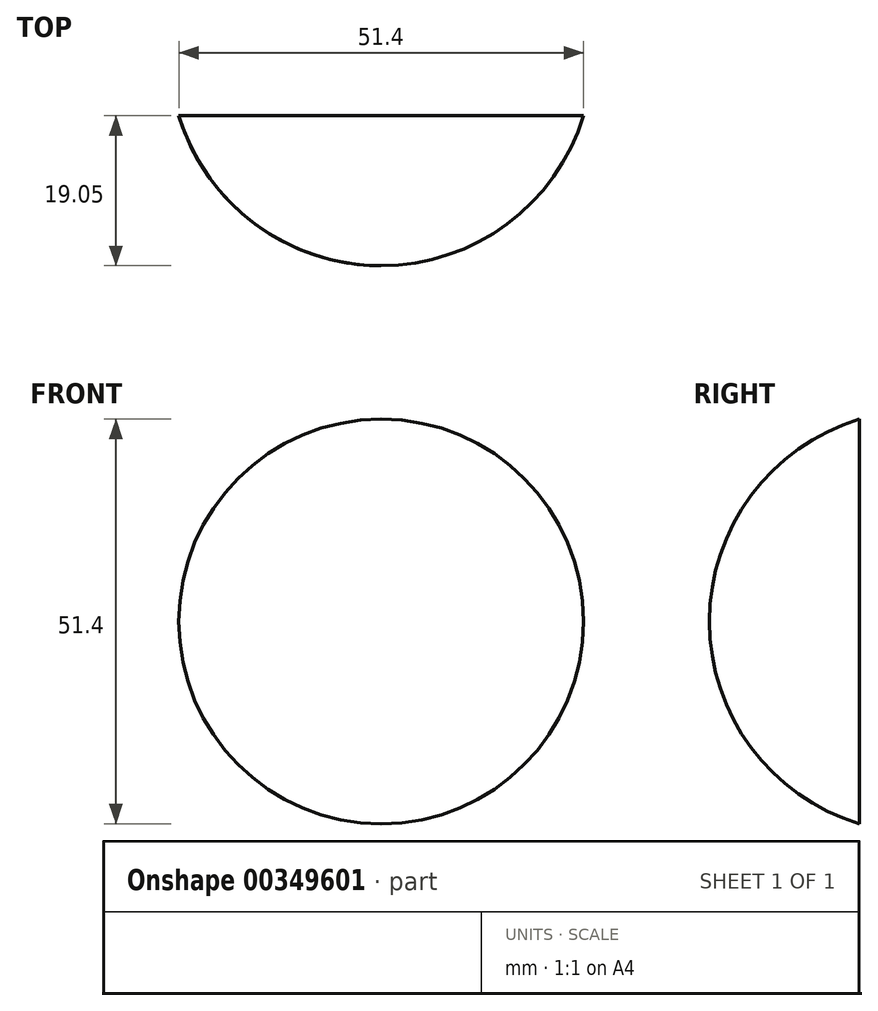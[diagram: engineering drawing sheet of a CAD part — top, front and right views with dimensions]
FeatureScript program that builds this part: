
annotation { "Feature Type Name" : "Feature", "Feature Type Description" : "" }
export const myFeature = defineFeature(function(context is Context, id is Id, definition is map)
    precondition{}
    {
        {
            var Q0;
            Q0=qCreatedBy(makeId("Front.planeOp"),FACE);
            var sketch = newSketch(context, id + "F0", { "sketchPlane" : qUnion([Q0])});
            skCircle(sketch, "E0", {"center": v(0, 0) * mm, "radius": 25.7 * mm});
            skLineSegment(sketch, "E1", {"start": v(-25.7, 0) * mm, "end": v(25.7, 0) * mm});
            skLineSegment(sketch, "E2", {"start": v(0, -25.7) * mm, "end": v(0, 25.7) * mm});
            skSolve(sketch);
        }
        {
            var Q0;
            Q0=qCreatedBy(makeId("Top.planeOp"),FACE);
            var sketch = newSketch(context, id + "F1", { "sketchPlane" : qUnion([Q0])});
            skLineSegment(sketch, "E3", {"start": v(0, 0) * mm, "end": v(0, -19.05) * mm});
            skPoint(sketch, "E4", {"position": v(-25.7, 0) * mm});
            skPoint(sketch, "E5", {"position": v(0, -19.05) * mm});
            skPoint(sketch, "E6", {"position": v(25.7, 0) * mm});
            skArc(sketch, "E7", {"start": v(-25.7, 0) * mm, "mid": v(-16, -13.77) * mm, "end": v(0, -19.05) * mm});
            skLineSegment(sketch, "E8", {"start": v(0, -19.05) * mm, "end": v(0, -44.45) * mm});
            skLineSegment(sketch, "E9", {"start": v(0, -19.05) * mm, "end": v(0, -19.05) * mm});
            skArc(sketch, "E10", {"start": v(0, -19.05) * mm, "mid": v(16, -13.77) * mm, "end": v(25.7, 0) * mm});
            skLineSegment(sketch, "E11", {"start": v(0, 0) * mm, "end": v(25.7, 0) * mm});
            skLineSegment(sketch, "E12", {"start": v(0, 0) * mm, "end": v(-25.7, 0) * mm});
            skSolve(sketch);
        }
        {
            var Q0;
            Q0=makeQuery(id+"F1.imprint","IMPRINT",FACE,{"disambiguationData":[TD([[makeQuery(id+"F1.imprint","IMPRINT",EDGE,{"derivedFrom":sQuery(id+"F1.wireOp",EDGE,"E3")}),-1.0]])]});
            var Q1;
            Q1=sQuery(id+"F1.wireOp",EDGE,"E3");
            revolve(context, id + "F2", {"entities" : qUnion([Q0]), "axis" : qUnion([Q1]), "revolveType" : RevolveType.FULL});
        }
    });
